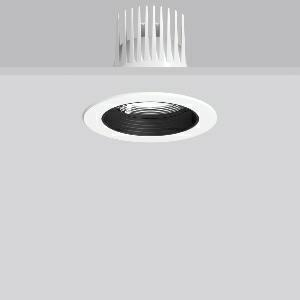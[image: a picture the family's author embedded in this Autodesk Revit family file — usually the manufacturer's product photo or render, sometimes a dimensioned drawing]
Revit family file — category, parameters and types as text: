
# Revit family: heledon_maxi_e_901760_002_1_76_fab7
name_source: partatom
category: Lighting Fixtures
units: mm (PartAtom-declared; Revit-internal decimal feet)

## family parameters
Cut with Voids When Loaded = No
Host = Face
Light Source = No
Part Type = Normal
Room Calculation Point = No
Round Connector Dimension = Use Diameter
Shared = No

## types (1)
- HELEDON maxi E (1 x LED Modul 940, 3000 lm, 4000)
    Apparent Load = 25 VA
    Approval mark = CE
    CIE Flux Codes = 97 100 100 100 100
    Color Rendering = 92
    Color Temperature = 4000
    Default Elevation = 1800 mm
    Description = Series: HELEDON maxi
Round recessed downlight. Housing: die-cast aluminium, powder-coated. Black plastic ring and recessed LED to prevent glare from the side. Optical assembly with lens made of plastic (polycarbonate) for the best homogeneous light distribution - can be changed without tools. Best colour rendering index Ra>90. Suitable for Recessed ceiling mounting. Installation without tools thanks to spring fastening system. Including separate LED converter with connecting cable 600 mm.High quality converter without flickering and stroboscopic effect. Through-wiring box (5 pole) available as accessory. The following accessories can be mounted without use of tools: interchangeable lenses, decorative glasses, honeycomb louvre, clear and frosted diffusers, white interchangeable plastic ring. 
Colour: traffic white, matt (RAL 9016)
Diameter: 162 mm
Height: 3 mm
Cut-out diameter: 152 mm
Recess height: 200 mm
Luminaire: recess height: 135 mm
Lamp: LED
Socket: without socket
Colour temperature: 4000K
Colour rendering index (CRI): 92
System power: 25 W
Rated luminous flux: 3000 lm
Luminous efficiency: 120 lm/W
Control gear: Converter, dimmable, DALI
Protection class: II
Type of protection: IP 20
    Height = 0 mm  [stored 0 ft]
    Lamp = 1 x LED Modul 940
    Lamp Light Flux = 3000 lm
    Lamp count = 1
    Length = 162 mm
    Lifetime = 50000 h
    Luminous efficacy = 120 lm/W
    Manufacturer = RZB
    ModVariant = No
    Model = 901760.002.1.76
    Mounting Place = Ceiling
    Mounting Type = Recessed
    Number of Poles = 1
    OnlyDefault = Yes
    Power Factor = 1
    Product Name = HELEDON maxi E
    Product group = Recessed downlights
    ProductGroupID = 402
    Protection Class = Protection class II
    Protection Degree = IP 20
    RLX_Detail_Level = 1
    RLX_Emergency_Light_Flux = 0 lm
    RLX_Emergency_Type = 0
    RLX_Emergency_Type_DB = No
    RlxData = <blob elided: 119313 chars, md5=bfa7d571>
    Socket = socket
    Standby Power = 0 W
    System Light Flux = 3000 lm
    System Power = 25 W
    Type Comments = Product without accessories
    Type Image = 901663.002.jpg
    URL = http://relux.com
    VarID = ---
    Voltage = 230 V
    Voltage Range = 220-240 V
    Weight = 0.00 kg
    Width = 0 mm  [stored 0 ft]

note: [stored X ft] marks values corroborated as IEEE doubles in the binary element streams (Revit-internal decimal feet)

## geometry (parser evidence)
native form markers: Blend x4, Sweep x10
no freeform markers — native parametric forms only
